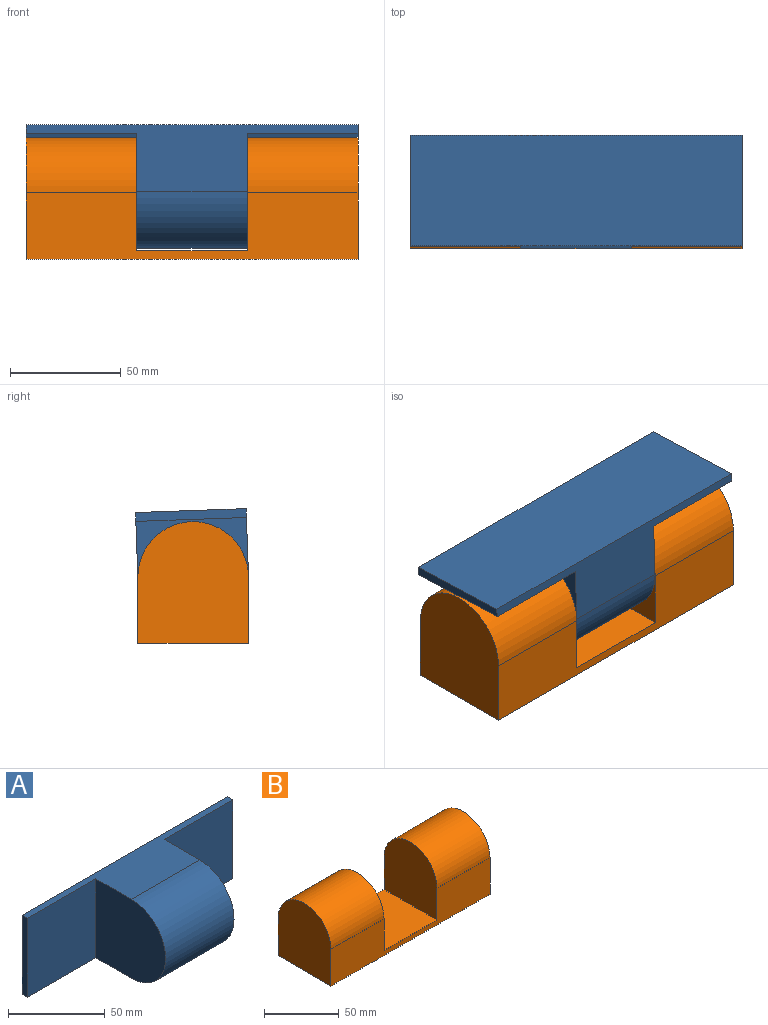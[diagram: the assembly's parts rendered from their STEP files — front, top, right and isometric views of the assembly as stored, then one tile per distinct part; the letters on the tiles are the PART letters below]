
ASSEMBLY  parts=2 mates=1
PART A: 10 faces, bbox 150x55x50 mm
  f0: plane 150x30mm, normal (0,0,1), area 1900mm2, adj f2,f3,f4,f5,f6,f7,f8,f9
  f1: plane 150x30mm, normal (0,0,-1), area 1900mm2, adj f2,f3,f4,f5,f6,f7,f8,f9
  f2: cylinder r=25mm len=50mm, axis (-1,0,0), area 3927mm2, adj f0,f1,f7,f9
  f3: plane 150x50mm, normal (0,1,0), area 7500mm2, adj f0,f1,f4,f5
  f4: plane 50x4mm, normal (1,0,0), area 200mm2, adj f0,f1,f3,f8
  f5: plane 50x4mm, normal (-1,0,0), area 200mm2, adj f0,f1,f3,f6
  f6: plane 50x50mm, normal (0,-1,0), area 2500mm2, adj f0,f1,f5,f7
  f7: plane 51x50mm, normal (-1,0,0), area 2281.7mm2, adj f0,f1,f2,f6
  f8: plane 50x50mm, normal (0,-1,0), area 2500mm2, adj f0,f1,f4,f9
  f9: plane 51x50mm, normal (1,0,0), area 2281.7mm2, adj f0,f1,f2,f8
PART B: 10 faces, bbox 150x50x55 mm
  f0: cylinder r=25mm len=50mm, axis (-1,0,0), area 3927mm2, adj f1,f2,f4,f9
  f1: plane 150x30mm, normal (0,1,0), area 3200mm2, adj f0,f3,f4,f5,f6,f7,f8,f9
  f2: plane 150x30mm, normal (0,-1,0), area 3200mm2, adj f0,f3,f4,f5,f6,f7,f8,f9
  f3: plane 150x50mm, normal (0,0,-1), area 7500mm2, adj f1,f2,f4,f5
  f4: plane 55x50mm, normal (1,0,0), area 2481.7mm2, adj f0,f1,f2,f3
  f5: plane 55x50mm, normal (-1,0,0), area 2481.7mm2, adj f1,f2,f3,f6
  f6: cylinder r=25mm len=50mm, axis (-1,0,0), area 3927mm2, adj f1,f2,f5,f8
  f7: plane 50x50mm, normal (0,0,1), area 2500mm2, adj f1,f2,f8,f9
  f8: plane 51x50mm, normal (1,0,0), area 2281.7mm2, adj f1,f2,f6,f7
  f9: plane 51x50mm, normal (-1,0,0), area 2281.7mm2, adj f0,f1,f2,f7
PLACE A rot(axis=(1,0,0),88deg) t=(0,-2.41,2.5)mm
PLACE B at identity fixed
MATE revolute A.f2 <-> B.f0  axis (-1,0,0) through (100,-2.5,0)mm
